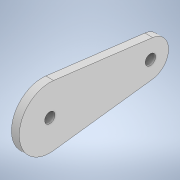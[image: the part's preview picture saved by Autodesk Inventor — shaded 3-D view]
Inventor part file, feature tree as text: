
AUTODESK INVENTOR PART (.ipt)
format: ipt  version: 2020 (Build 240168000, 168)  size: 146,944 bytes
history: native  units: mm
features: extrude x3, sketch x3, projected_geometry x1
ambient origin geometry x8: Origin, YZ Plane, XZ Plane, XY Plane, X Axis, Y Axis, Z Axis, Center Point
bodies: Body1 (feature_tree)
feature tree (7):
  extrude  "Выдавливание4"  Depth=18.6mm
  extrude  "Выдавливание5"  Depth=12.2mm
  extrude  "Выдавливание6"  Depth=9.7mm
  sketch  "Эскиз1"
  sketch  "Эскиз4"
  projected_geometry  "Спроецированная петля3"
  sketch  "Эскиз5"
